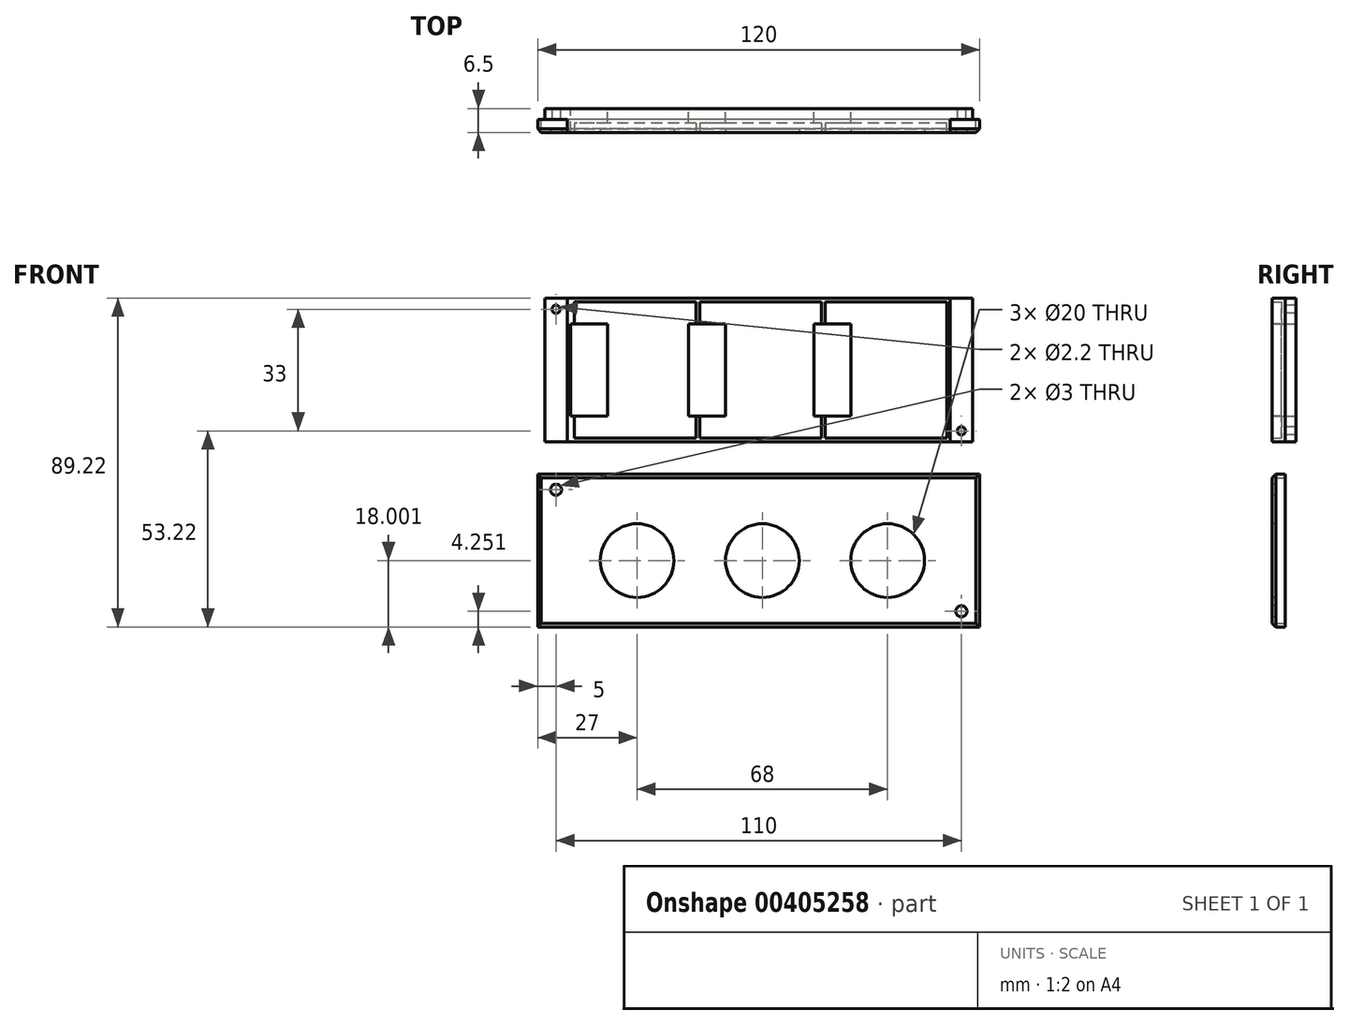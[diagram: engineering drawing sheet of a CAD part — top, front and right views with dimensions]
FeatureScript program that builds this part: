
annotation { "Feature Type Name" : "Feature", "Feature Type Description" : "" }
export const myFeature = defineFeature(function(context is Context, id is Id, definition is map)
    precondition{}
    {
        {
            var Q0;
            Q0=qCreatedBy(makeId("Front.planeOp"),FACE);
            var sketch = newSketch(context, id + "F0", { "sketchPlane" : qUnion([Q0])});
            skLineSegment(sketch, "E0.bottom", {"start": v(52, -19.5) * mm, "end": v(-52, -19.5) * mm});
            skLineSegment(sketch, "E0.top", {"start": v(52, 19.5) * mm, "end": v(-52, 19.5) * mm});
            skLineSegment(sketch, "E0.left", {"start": v(52, -19.5) * mm, "end": v(52, 19.5) * mm});
            skLineSegment(sketch, "E0.right", {"start": v(-52, -19.5) * mm, "end": v(-52, 19.5) * mm});
            skPoint(sketch, "E0.middle", {"position": v(0, 0) * mm});
            skSolve(sketch);
        }
        {
            var Q0;
            Q0=qSketchRegion(id+"F0",true);
            extrude(context, id + "F1", {"entities" : qUnion([Q0]), "depth" : 3.5 * mm});
        }
        {
            var Q0;
            Q0=makeQuery(id+"F1.opExtrude","CAP_FACE",FACE,{"disambiguationData":[OSD([sQuery(id+"F0.wireOp",EDGE,"E0.bottom"),sQuery(id+"F0.wireOp",EDGE,"E0.top"),sQuery(id+"F0.wireOp",EDGE,"E0.left"),sQuery(id+"F0.wireOp",EDGE,"E0.right")])],"isStart":false});
            shell(context, id + "F2", {"entities" : qUnion([Q0]), "thickness" : 1 * mm});
        }
        {
            var Q0;
            Q0=makeQuery(id+"F2.opShell","OFFSET_FACE",FACE,{"disambiguationData":[OSD([sQuery(id+"F0.wireOp",EDGE,"E0.bottom"),sQuery(id+"F0.wireOp",EDGE,"E0.top"),sQuery(id+"F0.wireOp",EDGE,"E0.left"),sQuery(id+"F0.wireOp",EDGE,"E0.right")])]});
            var sketch = newSketch(context, id + "F3", { "sketchPlane" : qUnion([Q0])});
            skLineSegment(sketch, "E1.bottom", {"start": v(-17, 18.5) * mm, "end": v(-16, 18.5) * mm});
            skLineSegment(sketch, "E1.top", {"start": v(-17, -18.5) * mm, "end": v(-16, -18.5) * mm});
            skLineSegment(sketch, "E1.left", {"start": v(-17, 18.5) * mm, "end": v(-17, -18.5) * mm});
            skLineSegment(sketch, "E1.right", {"start": v(-16, 18.5) * mm, "end": v(-16, -18.5) * mm});
            skLineSegment(sketch, "E2.bottom", {"start": v(17, 18.5) * mm, "end": v(18, 18.5) * mm});
            skLineSegment(sketch, "E2.top", {"start": v(17, -18.5) * mm, "end": v(18, -18.5) * mm});
            skLineSegment(sketch, "E2.left", {"start": v(17, 18.5) * mm, "end": v(17, -18.5) * mm});
            skLineSegment(sketch, "E2.right", {"start": v(18, 18.5) * mm, "end": v(18, -18.5) * mm});
            skLineSegment(sketch, "E3.bottom", {"start": v(-51, 18.5) * mm, "end": v(-50, 18.5) * mm});
            skLineSegment(sketch, "E3.top", {"start": v(-51, -18.5) * mm, "end": v(-50, -18.5) * mm});
            skLineSegment(sketch, "E3.left", {"start": v(-51, 18.5) * mm, "end": v(-51, -18.5) * mm});
            skLineSegment(sketch, "E3.right", {"start": v(-50, 18.5) * mm, "end": v(-50, -18.5) * mm});
            skSolve(sketch);
        }
        {
            var Q0;
            Q0=qSketchRegion(id+"F3",true);
            extrude(context, id + "F4", {"entities" : qUnion([Q0]), "operationType" : NewBodyOperationType.ADD, "depth" : 2.5 * mm});
        }
        {
            var Q0;
            Q0=makeQuery(id+"F1.opExtrude","CAP_FACE",FACE,{"disambiguationData":[OSD([sQuery(id+"F0.wireOp",EDGE,"E0.bottom"),sQuery(id+"F0.wireOp",EDGE,"E0.top"),sQuery(id+"F0.wireOp",EDGE,"E0.left"),sQuery(id+"F0.wireOp",EDGE,"E0.right")])],"isStart":true});
            var sketch = newSketch(context, id + "F5", { "sketchPlane" : qUnion([Q0])});
            skLineSegment(sketch, "E4.bottom", {"start": v(-58, 19.5) * mm, "end": v(58, 19.5) * mm});
            skLineSegment(sketch, "E4.top", {"start": v(-58, -19.5) * mm, "end": v(58, -19.5) * mm});
            skLineSegment(sketch, "E4.left", {"start": v(-58, 19.5) * mm, "end": v(-58, -19.5) * mm});
            skLineSegment(sketch, "E4.right", {"start": v(58, 19.5) * mm, "end": v(58, -19.5) * mm});
            skCircle(sketch, "E5", {"center": v(55, 16.5) * mm, "radius": 1.1 * mm});
            skCircle(sketch, "E6", {"center": v(55, -16.5) * mm, "radius": 1.1 * mm, "construction": true});
            skCircle(sketch, "E7", {"center": v(-55, 16.5) * mm, "radius": 1.1 * mm, "construction": true});
            skCircle(sketch, "E8", {"center": v(-55, -16.5) * mm, "radius": 1.1 * mm});
            skSolve(sketch);
        }
        {
            var Q0;
            Q0=qSketchRegion(id+"F5",true);
            extrude(context, id + "F6", {"entities" : qUnion([Q0]), "operationType" : NewBodyOperationType.ADD, "depth" : 3 * mm});
        }
        {
            var Q0;
            Q0=qCreatedBy(makeId("Front.planeOp"),FACE);
            var sketch = newSketch(context, id + "F7", { "sketchPlane" : qUnion([Q0])});
            skLineSegment(sketch, "E9.bottom", {"start": v(-51, 12.5) * mm, "end": v(-41, 12.5) * mm});
            skLineSegment(sketch, "E9.top", {"start": v(-51, -12.5) * mm, "end": v(-41, -12.5) * mm});
            skLineSegment(sketch, "E9.left", {"start": v(-51, 12.5) * mm, "end": v(-51, -12.5) * mm});
            skLineSegment(sketch, "E9.right", {"start": v(-41, 12.5) * mm, "end": v(-41, -12.5) * mm});
            skLineSegment(sketch, "E10.bottom", {"start": v(-19, 12.5) * mm, "end": v(-9, 12.5) * mm});
            skLineSegment(sketch, "E10.top", {"start": v(-19, -12.5) * mm, "end": v(-9, -12.5) * mm});
            skLineSegment(sketch, "E10.left", {"start": v(-19, 12.5) * mm, "end": v(-19, -12.5) * mm});
            skLineSegment(sketch, "E10.right", {"start": v(-9, 12.5) * mm, "end": v(-9, -12.5) * mm});
            skLineSegment(sketch, "E11.bottom", {"start": v(15, 12.5) * mm, "end": v(25, 12.5) * mm});
            skLineSegment(sketch, "E11.top", {"start": v(15, -12.5) * mm, "end": v(25, -12.5) * mm});
            skLineSegment(sketch, "E11.left", {"start": v(15, 12.5) * mm, "end": v(15, -12.5) * mm});
            skLineSegment(sketch, "E11.right", {"start": v(25, 12.5) * mm, "end": v(25, -12.5) * mm});
            skSolve(sketch);
        }
        {
            var Q0;
            Q0=qSketchRegion(id+"F7",true);
            extrude(context, id + "F8", {"entities" : qUnion([Q0]), "operationType" : NewBodyOperationType.REMOVE, "endBound" : BoundingType.SYMMETRIC, "depth" : 11.2 * mm});
        }
        {
            var Q0;
            Q0=qCreatedBy(makeId("Front.planeOp"),FACE);
            var sketch = newSketch(context, id + "F9", { "sketchPlane" : qUnion([Q0])});
            skLineSegment(sketch, "E12.bottom", {"start": v(60, -69.72) * mm, "end": v(-60, -69.72) * mm});
            skLineSegment(sketch, "E12.top", {"start": v(60, -28.22) * mm, "end": v(-60, -28.22) * mm});
            skLineSegment(sketch, "E12.left", {"start": v(60, -69.72) * mm, "end": v(60, -28.22) * mm});
            skLineSegment(sketch, "E12.right", {"start": v(-60, -69.72) * mm, "end": v(-60, -28.22) * mm});
            skPoint(sketch, "E12.middle", {"position": v(0, -48.97) * mm});
            skSolve(sketch);
        }
        {
            var Q0;
            Q0=qSketchRegion(id+"F9",true);
            extrude(context, id + "F10", {"entities" : qUnion([Q0]), "depth" : 3.5 * mm});
        }
        {
            var Q0;
            Q0=makeQuery(id+"F10.opExtrude","CAP_FACE",FACE,{"disambiguationData":[OSD([sQuery(id+"F9.wireOp",EDGE,"E12.bottom"),sQuery(id+"F9.wireOp",EDGE,"E12.top"),sQuery(id+"F9.wireOp",EDGE,"E12.left"),sQuery(id+"F9.wireOp",EDGE,"E12.right")])],"isStart":true});
            shell(context, id + "F11", {"entities" : qUnion([Q0]), "thickness" : 1 * mm});
        }
        {
            var Q0;
            Q0=makeQuery(id+"F10.opExtrude","CAP_FACE",FACE,{"disambiguationData":[OSD([sQuery(id+"F9.wireOp",EDGE,"E12.bottom"),sQuery(id+"F9.wireOp",EDGE,"E12.top"),sQuery(id+"F9.wireOp",EDGE,"E12.left"),sQuery(id+"F9.wireOp",EDGE,"E12.right")])],"isStart":false});
            var sketch = newSketch(context, id + "F12", { "sketchPlane" : qUnion([Q0])});
            skCircle(sketch, "E13", {"center": v(55, -65.47) * mm, "radius": 1.5 * mm});
            skCircle(sketch, "E14", {"center": v(-55, -32.47) * mm, "radius": 1.5 * mm});
            skCircle(sketch, "E15", {"center": v(-33, -51.72) * mm, "radius": 10 * mm});
            skCircle(sketch, "E16", {"center": v(1, -51.72) * mm, "radius": 10 * mm});
            skCircle(sketch, "E17", {"center": v(35, -51.72) * mm, "radius": 10 * mm});
            skSolve(sketch);
        }
        {
            var Q0;
            Q0=qSketchRegion(id+"F12",true);
            extrude(context, id + "F13", {"entities" : qUnion([Q0]), "operationType" : NewBodyOperationType.REMOVE, "oppositeDirection" : true, "depth" : 1 * mm});
        }
        {
            var Q0;
            Q0=makeQuery(id+"F10.opExtrude","CAP_EDGE",EDGE,{"disambiguationData":[OSD([sQuery(id+"F9.wireOp",EDGE,"E12.top")])],"isStart":false});
            var Q1;
            Q1=makeQuery(id+"F10.opExtrude","CAP_EDGE",EDGE,{"disambiguationData":[OSD([sQuery(id+"F9.wireOp",EDGE,"E12.right")])],"isStart":false});
            var Q2;
            Q2=makeQuery(id+"F10.opExtrude","CAP_EDGE",EDGE,{"disambiguationData":[OSD([sQuery(id+"F9.wireOp",EDGE,"E12.left")])],"isStart":false});
            var Q3;
            Q3=makeQuery(id+"F10.opExtrude","CAP_EDGE",EDGE,{"disambiguationData":[OSD([sQuery(id+"F9.wireOp",EDGE,"E12.bottom")])],"isStart":false});
            chamfer(context, id + "F14", {"entities" : qUnion([Q0, Q1, Q2, Q3]), "width" : 1 * mm, "tangentPropagation" : true});
        }
    });
